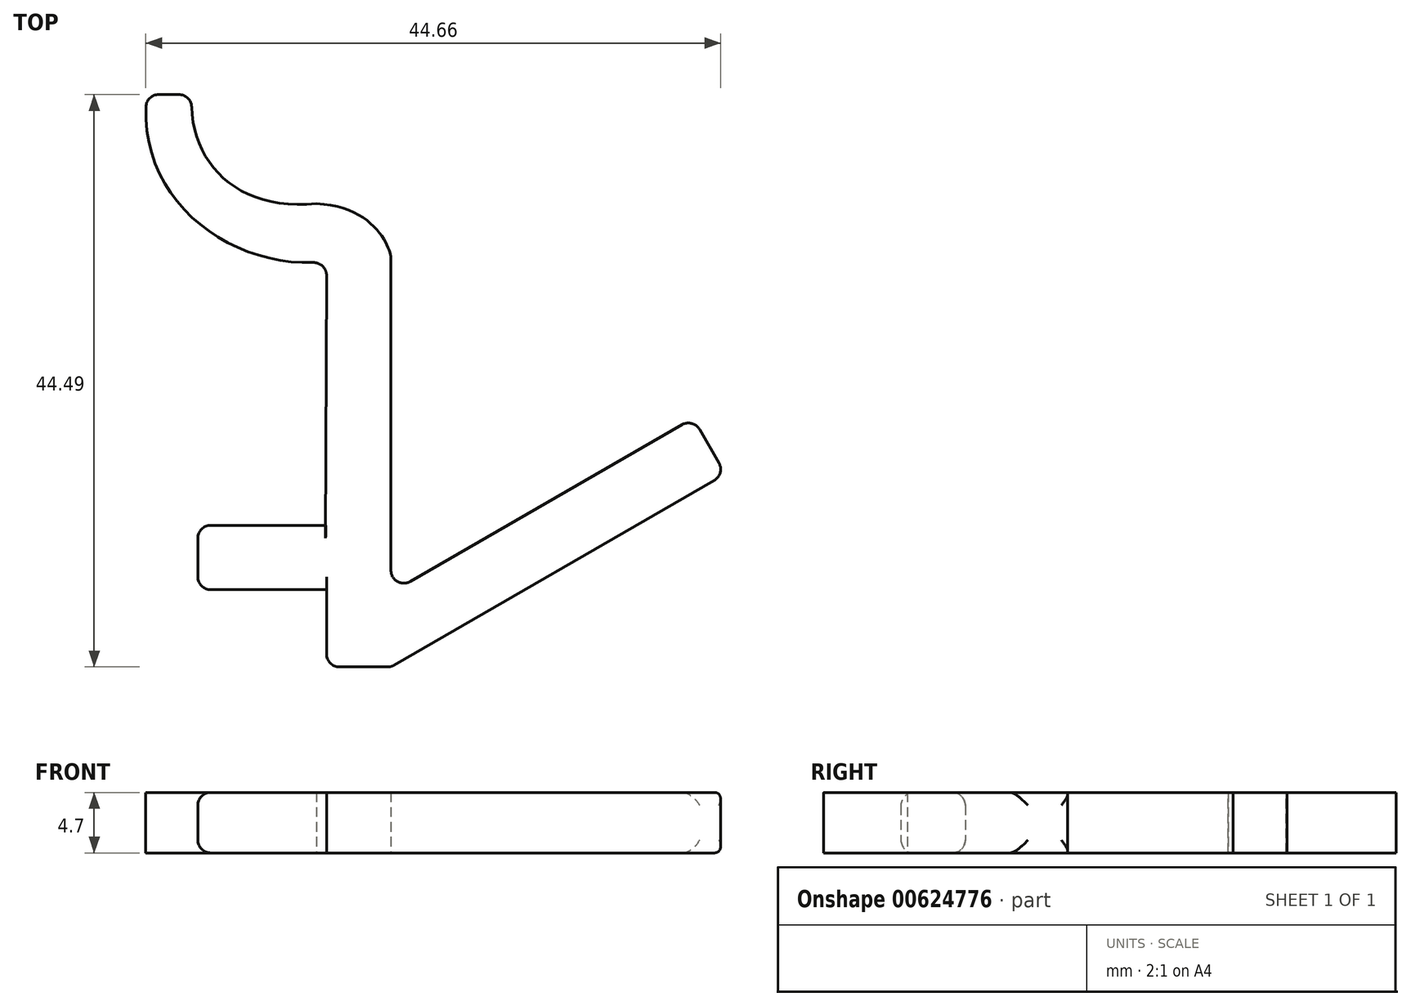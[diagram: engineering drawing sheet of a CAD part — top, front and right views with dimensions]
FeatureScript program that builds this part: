
annotation { "Feature Type Name" : "Feature", "Feature Type Description" : "" }
export const myFeature = defineFeature(function(context is Context, id is Id, definition is map)
    precondition{}
    {
        {
            var Q0;
            Q0=qCreatedBy(makeId("Top.planeOp"),FACE);
            var sketch = newSketch(context, id + "F0", { "sketchPlane" : qUnion([Q0])});
            skLineSegment(sketch, "E0", {"start": v(-41.36, 16.6) * mm, "end": v(-37.86, 16.6) * mm});
            skFitSpline(sketch, "E1", {"points": [v(-37.86, 16.6) * mm, v(-28.18, 8.11) * mm], "startDerivative": vector(-1.06, -15.17) * mm, "endDerivative": vector(19.05, 1.96) * mm});
            skFitSpline(sketch, "E2", {"points": [v(-28.18, 8.11) * mm, v(-22.4, 3.9) * mm], "startDerivative": vector(13.6, -0.54) * mm, "endDerivative": vector(0.17, -2.2) * mm});
            skFitSpline(sketch, "E3", {"points": [v(-41.36, 16.6) * mm, v(-27.4, 3.61) * mm], "startDerivative": vector(-2.9, -24.56) * mm, "endDerivative": vector(21.9, 2.52) * mm});
            skLineSegment(sketch, "E4", {"start": v(-22.4, 3.9) * mm, "end": v(-22.4, -27.9) * mm});
            skLineSegment(sketch, "E5", {"start": v(-22.4, -27.9) * mm, "end": v(-27.4, -27.9) * mm});
            skLineSegment(sketch, "E6", {"start": v(-27.4, -27.9) * mm, "end": v(-27.4, -21.89) * mm});
            skLineSegment(sketch, "E7", {"start": v(-27.4, -21.89) * mm, "end": v(-37.4, -21.89) * mm});
            skLineSegment(sketch, "E8", {"start": v(-37.4, -21.89) * mm, "end": v(-37.4, -16.89) * mm});
            skLineSegment(sketch, "E9", {"start": v(-37.4, -16.89) * mm, "end": v(-27.47, -16.89) * mm});
            skLineSegment(sketch, "E10", {"start": v(-27.47, -16.89) * mm, "end": v(-27.4, 3.61) * mm});
            skLineSegment(sketch, "E11", {"start": v(-22.4, -27.9) * mm, "end": v(3.58, -12.9) * mm});
            skLineSegment(sketch, "E12", {"start": v(3.58, -12.9) * mm, "end": v(1.08, -8.57) * mm});
            skLineSegment(sketch, "E13", {"start": v(1.08, -8.57) * mm, "end": v(-22.4, -22.12) * mm});
            skSolve(sketch);
        }
        {
            var Q0;
            Q0 = qSketchRegion(id + "F0", true);
            extrude(context, id + "F1", {"entities" : qUnion([Q0]), "depth" : 4.7 * mm, "offsetDistance" : 25 * mm});
        }
        {
            var Q0;
            Q0=makeQuery(id+"F1.opExtrude","CAP_EDGE",EDGE,{"disambiguationData":[OSD([sQuery(id+"F0.wireOp",EDGE,"E9")])],"isStart":false});
            var Q1;
            Q1=makeQuery(id+"F1.opExtrude","CAP_EDGE",EDGE,{"disambiguationData":[OSD([sQuery(id+"F0.wireOp",EDGE,"E9")])],"isStart":true});
            var Q2;
            Q2=makeQuery(id+"F1.opExtrude","CAP_EDGE",EDGE,{"disambiguationData":[OSD([sQuery(id+"F0.wireOp",EDGE,"E7")])],"isStart":false});
            var Q3;
            Q3=makeQuery(id+"F1.opExtrude","CAP_EDGE",EDGE,{"disambiguationData":[OSD([sQuery(id+"F0.wireOp",EDGE,"E7")])],"isStart":true});
            fillet(context, id + "F2", {"entities" : qUnion([Q0, Q1, Q2, Q3]), "radius" : 1 * mm, "tangentPropagation" : true, "allowEdgeOverflow" : false});
        }
        {
            var Q0;
            Q0=makeQuery(id+"F1.opExtrude","SWEPT_EDGE",EDGE,{"disambiguationData":[OSD([sQuery(id+"F0.wireOp",EDGE,"E5"),sQuery(id+"F0.wireOp",EDGE,"E6")])]});
            var Q1;
            Q1=makeQuery(id+"F1.opExtrude","SWEPT_EDGE",EDGE,{"disambiguationData":[OSD([sQuery(id+"F0.wireOp",EDGE,"E3"),sQuery(id+"F0.wireOp",EDGE,"E10")])]});
            fillet(context, id + "F3", {"entities" : qUnion([Q0, Q1]), "radius" : 1 * mm, "tangentPropagation" : true, "allowEdgeOverflow" : false});
        }
        {
            var Q0;
            Q0=makeQuery(id+"F1.opExtrude","SWEPT_EDGE",EDGE,{"disambiguationData":[OSD([sQuery(id+"F0.wireOp",EDGE,"E0"),sQuery(id+"F0.wireOp",EDGE,"E3")])]});
            var Q1;
            Q1=makeQuery(id+"F1.opExtrude","SWEPT_EDGE",EDGE,{"disambiguationData":[OSD([sQuery(id+"F0.wireOp",EDGE,"E0"),sQuery(id+"F0.wireOp",EDGE,"E1")])]});
            fillet(context, id + "F4", {"entities" : qUnion([Q0, Q1]), "radius" : 1 * mm, "tangentPropagation" : true, "allowEdgeOverflow" : false});
        }
        {
            var Q0;
            Q0=makeQuery(id+"F1.opExtrude","SWEPT_EDGE",EDGE,{"disambiguationData":[OSD([sQuery(id+"F0.wireOp",EDGE,"E4"),sQuery(id+"F0.wireOp",EDGE,"E13")])]});
            var Q1;
            Q1=makeQuery(id+"F1.opExtrude","SWEPT_EDGE",EDGE,{"disambiguationData":[OSD([sQuery(id+"F0.wireOp",EDGE,"E12"),sQuery(id+"F0.wireOp",EDGE,"E13")])]});
            var Q2;
            Q2=makeQuery(id+"F1.opExtrude","SWEPT_EDGE",EDGE,{"disambiguationData":[OSD([sQuery(id+"F0.wireOp",EDGE,"E11"),sQuery(id+"F0.wireOp",EDGE,"E12")])]});
            var Q3;
            Q3=makeQuery(id+"F1.opExtrude","CAP_EDGE",EDGE,{"disambiguationData":[OSD([sQuery(id+"F0.wireOp",EDGE,"E12")])],"isStart":true});
            var Q4;
            Q4=makeQuery(id+"F1.opExtrude","CAP_EDGE",EDGE,{"disambiguationData":[OSD([sQuery(id+"F0.wireOp",EDGE,"E12")])],"isStart":false});
            fillet(context, id + "F5", {"entities" : qUnion([Q0, Q1, Q2, Q3, Q4]), "radius" : 1 * mm, "tangentPropagation" : true, "allowEdgeOverflow" : false});
        }
        {
            var Q0;
            Q0=makeQuery(id+"F1.opExtrude","SWEPT_FACE",FACE,{"disambiguationData":[OSD([sQuery(id+"F0.wireOp",EDGE,"E8")])]});
            fillet(context, id + "F6", {"entities" : qUnion([Q0]), "radius" : 1 * mm, "tangentPropagation" : true, "allowEdgeOverflow" : false});
        }
        {
            var Q0;
            Q0=makeQuery(id+"F1.opExtrude","SWEPT_EDGE",EDGE,{"disambiguationData":[OSD([sQuery(id+"F0.wireOp",EDGE,"E4"),sQuery(id+"F0.wireOp",EDGE,"E5"),sQuery(id+"F0.wireOp",EDGE,"E11")])]});
            fillet(context, id + "F7", {"entities" : qUnion([Q0]), "radius" : 1 * mm, "tangentPropagation" : true, "allowEdgeOverflow" : false});
        }
    });
